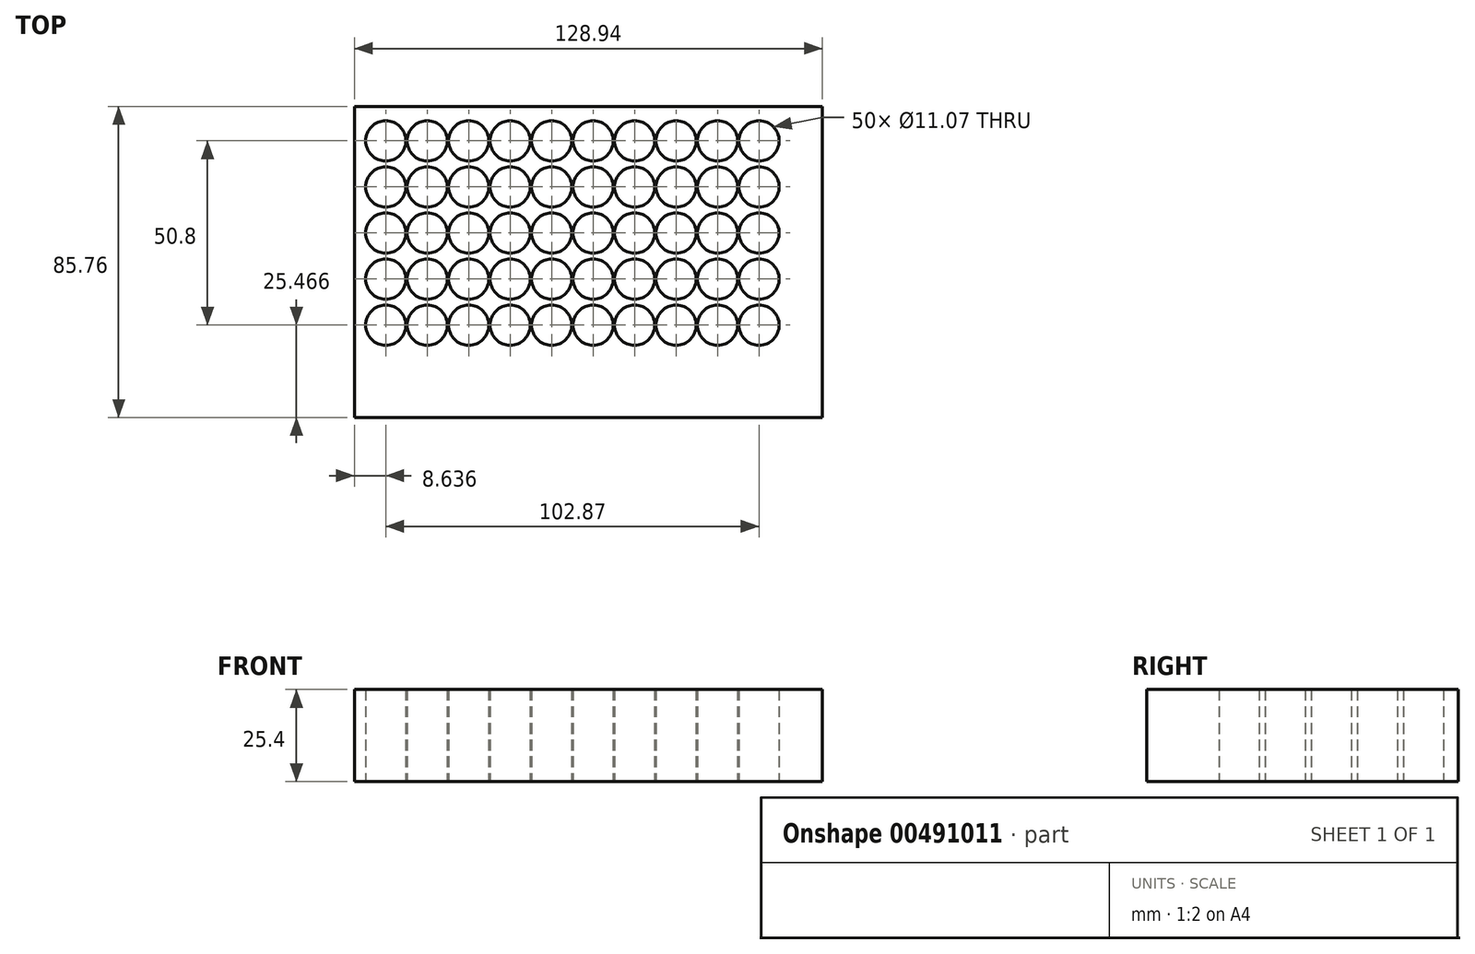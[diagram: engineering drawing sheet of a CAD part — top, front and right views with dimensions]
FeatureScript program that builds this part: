
annotation { "Feature Type Name" : "Feature", "Feature Type Description" : "" }
export const myFeature = defineFeature(function(context is Context, id is Id, definition is map)
    precondition{}
    {
        {
            var Q0;
            Q0=qCreatedBy(makeId("Top.planeOp"),FACE);
            var sketch = newSketch(context, id + "F0", { "sketchPlane" : qUnion([Q0])});
            skLineSegment(sketch, "E0.bottom", {"start": v(64.47, 42.88) * mm, "end": v(-64.47, 42.88) * mm});
            skLineSegment(sketch, "E0.top", {"start": v(64.47, -42.88) * mm, "end": v(-64.47, -42.88) * mm});
            skLineSegment(sketch, "E0.left", {"start": v(64.47, 42.88) * mm, "end": v(64.47, -42.88) * mm});
            skLineSegment(sketch, "E0.right", {"start": v(-64.47, 42.88) * mm, "end": v(-64.47, -42.88) * mm});
            skPoint(sketch, "E0.middle", {"position": v(0, 0) * mm});
            skCircle(sketch, "E1", {"center": v(-55.83, 33.39) * mm, "radius": 5.54 * mm});
            skCircle(sketch, "E2.0.1.0", {"center": v(-55.83, 20.69) * mm, "radius": 5.54 * mm});
            skCircle(sketch, "E2.0.2.0", {"center": v(-55.83, 7.99) * mm, "radius": 5.54 * mm});
            skCircle(sketch, "E2.0.3.0", {"center": v(-55.83, -4.71) * mm, "radius": 5.54 * mm});
            skCircle(sketch, "E2.0.4.0", {"center": v(-55.83, -17.41) * mm, "radius": 5.54 * mm});
            skCircle(sketch, "E2.1.0.0", {"center": v(-44.4, 33.39) * mm, "radius": 5.54 * mm});
            skCircle(sketch, "E2.1.1.0", {"center": v(-44.4, 20.69) * mm, "radius": 5.54 * mm});
            skCircle(sketch, "E2.1.2.0", {"center": v(-44.4, 7.99) * mm, "radius": 5.54 * mm});
            skCircle(sketch, "E2.1.3.0", {"center": v(-44.4, -4.71) * mm, "radius": 5.54 * mm});
            skCircle(sketch, "E2.1.4.0", {"center": v(-44.4, -17.41) * mm, "radius": 5.54 * mm});
            skCircle(sketch, "E2.2.0.0", {"center": v(-32.97, 33.39) * mm, "radius": 5.54 * mm});
            skCircle(sketch, "E2.2.1.0", {"center": v(-32.97, 20.69) * mm, "radius": 5.54 * mm});
            skCircle(sketch, "E2.2.2.0", {"center": v(-32.97, 7.99) * mm, "radius": 5.54 * mm});
            skCircle(sketch, "E2.2.3.0", {"center": v(-32.97, -4.71) * mm, "radius": 5.54 * mm});
            skCircle(sketch, "E2.2.4.0", {"center": v(-32.97, -17.41) * mm, "radius": 5.54 * mm});
            skCircle(sketch, "E2.3.0.0", {"center": v(-21.54, 33.39) * mm, "radius": 5.54 * mm});
            skCircle(sketch, "E2.3.1.0", {"center": v(-21.54, 20.69) * mm, "radius": 5.54 * mm});
            skCircle(sketch, "E2.3.2.0", {"center": v(-21.54, 7.99) * mm, "radius": 5.54 * mm});
            skCircle(sketch, "E2.3.3.0", {"center": v(-21.54, -4.71) * mm, "radius": 5.54 * mm});
            skCircle(sketch, "E2.3.4.0", {"center": v(-21.54, -17.41) * mm, "radius": 5.54 * mm});
            skCircle(sketch, "E2.4.0.0", {"center": v(-10.11, 33.39) * mm, "radius": 5.54 * mm});
            skCircle(sketch, "E2.4.1.0", {"center": v(-10.11, 20.69) * mm, "radius": 5.54 * mm});
            skCircle(sketch, "E2.4.2.0", {"center": v(-10.11, 7.99) * mm, "radius": 5.54 * mm});
            skCircle(sketch, "E2.4.3.0", {"center": v(-10.11, -4.71) * mm, "radius": 5.54 * mm});
            skCircle(sketch, "E2.4.4.0", {"center": v(-10.11, -17.41) * mm, "radius": 5.54 * mm});
            skCircle(sketch, "E2.5.0.0", {"center": v(1.32, 33.39) * mm, "radius": 5.54 * mm});
            skCircle(sketch, "E2.5.1.0", {"center": v(1.32, 20.69) * mm, "radius": 5.54 * mm});
            skCircle(sketch, "E2.5.2.0", {"center": v(1.32, 7.99) * mm, "radius": 5.54 * mm});
            skCircle(sketch, "E2.5.3.0", {"center": v(1.32, -4.71) * mm, "radius": 5.54 * mm});
            skCircle(sketch, "E2.5.4.0", {"center": v(1.32, -17.41) * mm, "radius": 5.54 * mm});
            skCircle(sketch, "E2.6.0.0", {"center": v(12.75, 33.39) * mm, "radius": 5.54 * mm});
            skCircle(sketch, "E2.6.1.0", {"center": v(12.75, 20.69) * mm, "radius": 5.54 * mm});
            skCircle(sketch, "E2.6.2.0", {"center": v(12.75, 7.99) * mm, "radius": 5.54 * mm});
            skCircle(sketch, "E2.6.3.0", {"center": v(12.75, -4.71) * mm, "radius": 5.54 * mm});
            skCircle(sketch, "E2.6.4.0", {"center": v(12.75, -17.41) * mm, "radius": 5.54 * mm});
            skCircle(sketch, "E2.7.0.0", {"center": v(24.18, 33.39) * mm, "radius": 5.54 * mm});
            skCircle(sketch, "E2.7.1.0", {"center": v(24.18, 20.69) * mm, "radius": 5.54 * mm});
            skCircle(sketch, "E2.7.2.0", {"center": v(24.18, 7.99) * mm, "radius": 5.54 * mm});
            skCircle(sketch, "E2.7.3.0", {"center": v(24.18, -4.71) * mm, "radius": 5.54 * mm});
            skCircle(sketch, "E2.7.4.0", {"center": v(24.18, -17.41) * mm, "radius": 5.54 * mm});
            skCircle(sketch, "E2.8.0.0", {"center": v(35.6, 33.39) * mm, "radius": 5.54 * mm});
            skCircle(sketch, "E2.8.1.0", {"center": v(35.6, 20.69) * mm, "radius": 5.54 * mm});
            skCircle(sketch, "E2.8.2.0", {"center": v(35.6, 7.99) * mm, "radius": 5.54 * mm});
            skCircle(sketch, "E2.8.3.0", {"center": v(35.6, -4.71) * mm, "radius": 5.54 * mm});
            skCircle(sketch, "E2.8.4.0", {"center": v(35.6, -17.41) * mm, "radius": 5.54 * mm});
            skCircle(sketch, "E2.9.0.0", {"center": v(47.04, 33.39) * mm, "radius": 5.54 * mm});
            skCircle(sketch, "E2.9.1.0", {"center": v(47.04, 20.69) * mm, "radius": 5.54 * mm});
            skCircle(sketch, "E2.9.2.0", {"center": v(47.04, 7.99) * mm, "radius": 5.54 * mm});
            skCircle(sketch, "E2.9.3.0", {"center": v(47.04, -4.71) * mm, "radius": 5.54 * mm});
            skCircle(sketch, "E2.9.4.0", {"center": v(47.04, -17.41) * mm, "radius": 5.54 * mm});
            skLineSegment(sketch, "E2.direction1", {"start": v(-55.83, 33.39) * mm, "end": v(-44.4, 33.39) * mm, "construction": true});
            skLineSegment(sketch, "E2.direction2", {"start": v(-55.83, 33.39) * mm, "end": v(-55.83, 20.69) * mm, "construction": true});
            skSolve(sketch);
        }
        {
            var Q0;
            Q0 = qSketchRegion(id + "F0", true);
            extrude(context, id + "F1", {"entities" : qUnion([Q0]), "depth" : 25.4 * mm});
        }
    });
